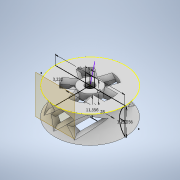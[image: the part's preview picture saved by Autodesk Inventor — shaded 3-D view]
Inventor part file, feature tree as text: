
AUTODESK INVENTOR PART (.ipt)
format: ipt  version: 2020 (Build 240168000, 168)  size: 447,488 bytes
history: native  units: mm
features: sketch x4, revolve x2, extrude x2, chamfer x2, plane x1
ambient origin geometry x8: Origin, YZ Plane, XZ Plane, XY Plane, X Axis, Y Axis, Z Axis, Center Point
bodies: Solid1 (feature_tree)
feature tree (11):
  sketch  "Sketch1"  dims[d0=15.556349mm d1=40.0mm]
  revolve  "Revolution1"  [1 undecoded]
  revolve  "Revolution2"  [1 undecoded]
  sketch  "Sketch2"  dims[d2=3.222mm d3=3.222mm]
  plane  "Work Plane1"
  extrude  "Extrusion1"  Depth=28.0mm
  chamfer  "Chamfer1"  Distance=5.0mm
  extrude  "Extrusion2"  Depth=10.0mm
  chamfer  "Chamfer2"  Angle=90.0deg  [1 undecoded]
  sketch  "Sketch3"  dims[d4=90.0deg d5=28.0mm]
  sketch  "Sketch4"  dims[d6=11.556mm d7=5.0mm d8=13.0mm d9=90.0deg d10=12.0mm d11=45.0deg d12=3.0mm d13=20.0mm d15=10.0mm d16=20.0mm d18=10.0mm d21=0.0mm d22=0.0mm d23=2.0mm d24=2.0mm d25=45.0deg d26=12.0mm d27=25.0mm d28=50.0mm d30=360.0deg d32=10.0mm d33=0.0mm d34=2.0mm d35=2.0mm d36=45.0deg]
note: 3 required parameter values undecoded (feature->parameter linkage not recoverable at this tier; creation-order binding heuristic only, values carry confidence <= 0.55)